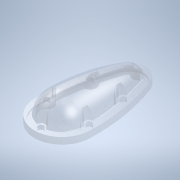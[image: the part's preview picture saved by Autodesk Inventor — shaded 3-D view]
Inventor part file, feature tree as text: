
AUTODESK INVENTOR PART (.ipt)
format: ipt  version: 2022 (Build 260153000, 153)  size: 577,536 bytes
history: native  units: mm
features: other x4, extrude x4, sketch x2, fillet x2, pattern_linear x2, shell x1, hole x1
ambient origin geometry x8: Origin, YZ Plane, XZ Plane, XY Plane, X Axis, Y Axis, Z Axis, Center Point
bodies: Body1 (feature_tree)
feature tree (16):
  other  "Těleso1"
  sketch  "Náčrt1"
  other  "Rotace1"
  shell  "Skořepina1"  Thickness=100.0mm
  extrude  "Vysunutí1"  Depth=130.0mm
  sketch  "Náčrt2"
  extrude  "Vysunutí2"  Depth=50.0mm
  other  "PlochaZešikmení1"
  other  "Pero1"
  extrude  "Vysunutí3"  Depth=80.0mm
  hole  "Díra1"  [1 undecoded]
  extrude  "Vysunutí4"  Depth=436.0mm
  fillet  "Zaoblení1"  Radius=488.0mm
  pattern_linear  "Obdélníkové pole1"  Spacing1=19.5mm  [1 undecoded]
  pattern_linear  "Obdélníkové pole2"  Spacing1=180.0deg  [1 undecoded]
  fillet  "Zaoblení2"  Radius=5.0mm
note: 3 required parameter values undecoded (feature->parameter linkage not recoverable at this tier; creation-order binding heuristic only, values carry confidence <= 0.55)
